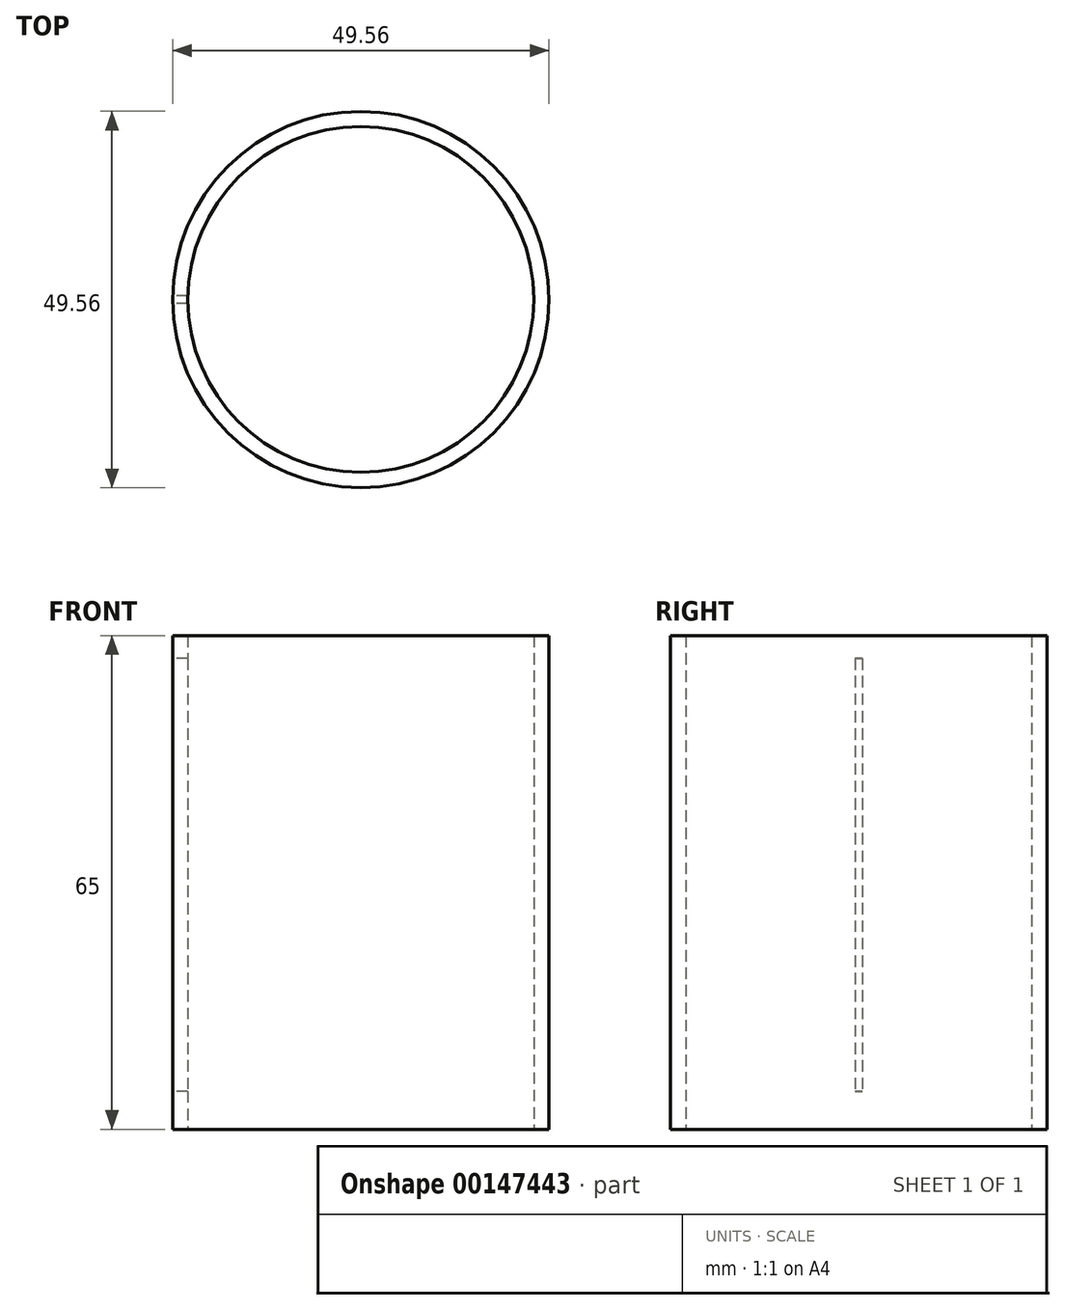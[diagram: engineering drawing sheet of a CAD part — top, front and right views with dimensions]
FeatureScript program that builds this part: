
annotation { "Feature Type Name" : "Feature", "Feature Type Description" : "" }
export const myFeature = defineFeature(function(context is Context, id is Id, definition is map)
    precondition{}
    {
        {
            var Q0;
            Q0=qCreatedBy(makeId("Top.planeOp"),FACE);
            var sketch = newSketch(context, id + "F0", { "sketchPlane" : qUnion([Q0])});
            skCircle(sketch, "E0", {"center": v(0, 0) * mm, "radius": 22.77 * mm});
            skCircle(sketch, "E1", {"center": v(0, 0) * mm, "radius": 24.77 * mm});
            skSolve(sketch);
        }
        {
            var Q0;
            Q0=makeQuery(id+"F0.imprint","IMPRINT",FACE,{"disambiguationData":[TD([[makeQuery(id+"F0.imprint","IMPRINT",EDGE,{"derivedFrom":sQuery(id+"F0.wireOp",EDGE,"E0")}),-1.0]])]});
            extrude(context, id + "F1", {"entities" : qUnion([Q0]), "depth" : 65 * mm});
        }
        {
            var Q0;
            Q0=qCreatedBy(makeId("Top.planeOp"),FACE);
            cPlane(context, id + "F2", {"entities" : qUnion([Q0]), "cplaneType" : CPlaneType.OFFSET, "offset" : 5 * mm, "width" : 150 * mm, "height" : 150 * mm});
        }
        {
            var Q0;
            Q0=qCreatedBy(id+"F2.planeOp",FACE);
            var sketch = newSketch(context, id + "F3", { "sketchPlane" : qUnion([Q0])});
            skLineSegment(sketch, "E2.bottom", {"start": v(-22.77, -0.5) * mm, "end": v(-24.77, -0.5) * mm});
            skLineSegment(sketch, "E2.top", {"start": v(-22.77, 0.5) * mm, "end": v(-24.77, 0.5) * mm});
            skLineSegment(sketch, "E2.left", {"start": v(-22.77, -0.5) * mm, "end": v(-22.77, 0.5) * mm});
            skLineSegment(sketch, "E2.right", {"start": v(-24.77, -0.5) * mm, "end": v(-24.77, 0.5) * mm});
            skSolve(sketch);
        }
        {
            var Q0;
            Q0=sQuery(id+"F3.wireOp",EDGE,"E2.bottom");
            var Q1;
            Q1=sQuery(id+"F3.wireOp",EDGE,"E2.left");
            var Q2;
            Q2=sQuery(id+"F3.wireOp",EDGE,"E2.right");
            extrude(context, id + "F4", {"bodyType" : ToolBodyType.SURFACE, "operationType" : NewBodyOperationType.REMOVE, "surfaceEntities" : qUnion([Q0, Q1, Q2]), "depth" : 57 * mm});
        }
        {
            var Q0;
            Q0=makeQuery(id+"F4.opExtrude","SWEPT_FACE",FACE,{"disambiguationData":[OSD([sQuery(id+"F3.wireOp",EDGE,"E2.right")])]});
            extrude(context, id + "F5", {"entities" : qUnion([Q0]), "operationType" : NewBodyOperationType.REMOVE, "depth" : 20 * mm});
        }
    });
